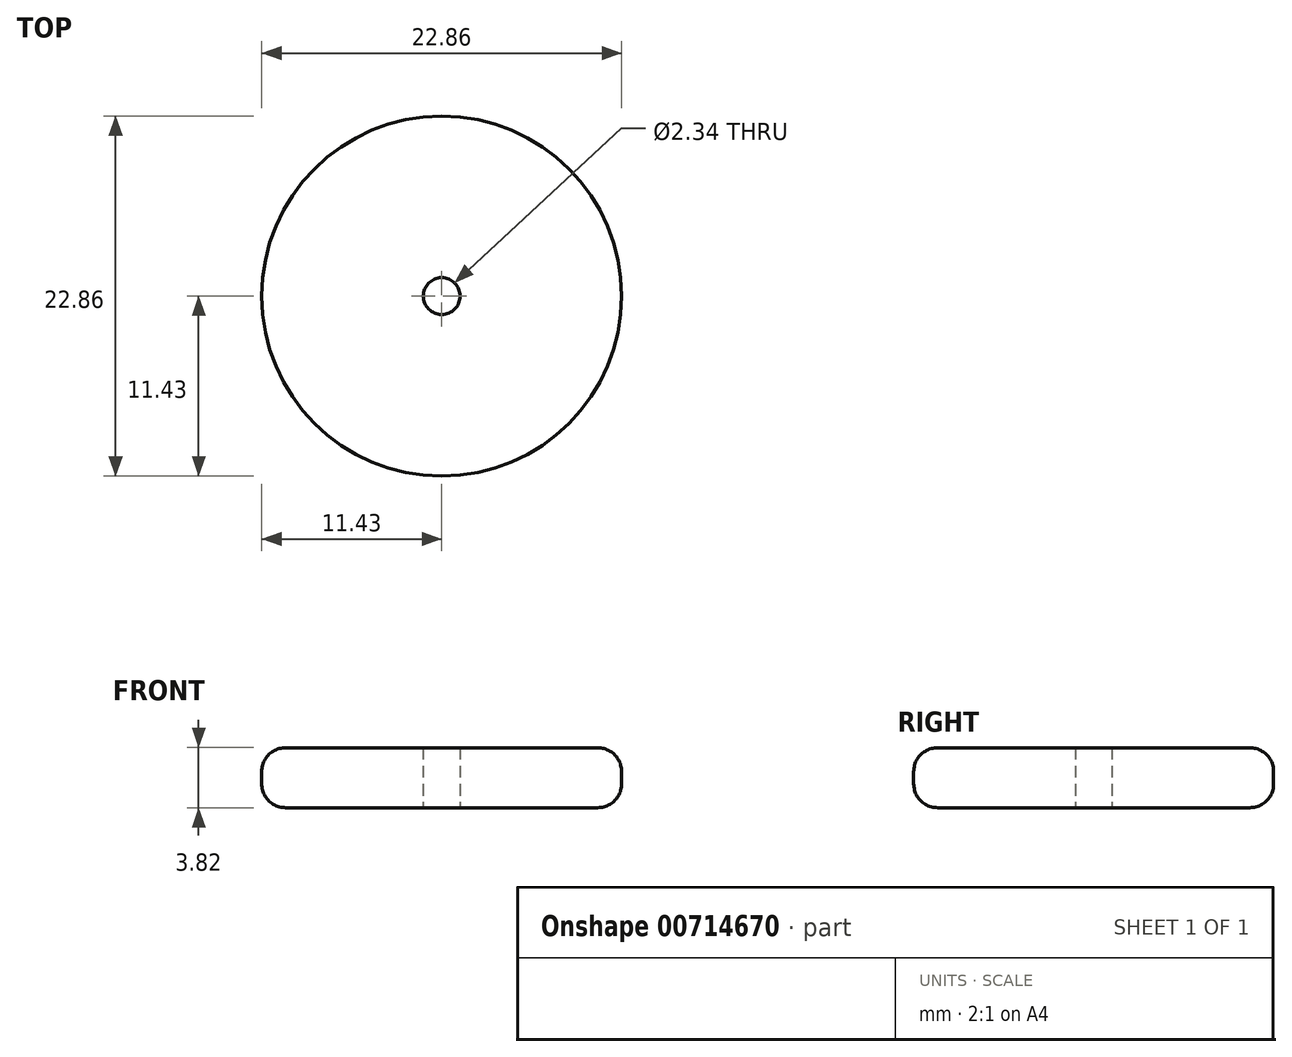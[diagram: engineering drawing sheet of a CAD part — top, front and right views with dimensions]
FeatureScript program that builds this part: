
annotation { "Feature Type Name" : "Feature", "Feature Type Description" : "" }
export const myFeature = defineFeature(function(context is Context, id is Id, definition is map)
    precondition{}
    {
        {
            var Q0;
            Q0=qCreatedBy(makeId("Top.planeOp"),FACE);
            var sketch = newSketch(context, id + "F0", { "sketchPlane" : qUnion([Q0])});
            skPoint(sketch, "E0.center.orphan", {"position": v(0, 0) * mm});
            skPoint(sketch, "E1.start.orphan", {"position": v(11.43, 0) * mm});
            skCircle(sketch, "E2", {"center": v(0, 0) * mm, "radius": 11.43 * mm});
            skSolve(sketch);
        }
        {
            var Q0;
            Q0 = qSketchRegion(id + "F0", true);
            extrude(context, id + "F1", {"entities" : qUnion([Q0]), "depth" : 3.8 * mm, "offsetDistance" : 25.4 * mm, "symmetric" : true});
        }
        {
            var Q0;
            Q0=makeQuery(id+"F1.opExtrude","CAP_FACE",FACE,{"disambiguationData":[OSD([sQuery(id+"F0.wireOp",EDGE,"E2")])],"isStart":true});
            var sketch = newSketch(context, id + "F2", { "sketchPlane" : qUnion([Q0])});
            skCircle(sketch, "E3", {"center": v(0, 0) * mm, "radius": 1.17 * mm});
            skSolve(sketch);
        }
        {
            var Q0;
            Q0=makeQuery(id+"F2.imprint","IMPRINT",FACE,{"disambiguationData":[TD([[makeQuery(id+"F2.imprint","IMPRINT",EDGE,{"derivedFrom":sQuery(id+"F2.wireOp",EDGE,"E3")}),1.0]])]});
            extrude(context, id + "F3", {"entities" : qUnion([Q0]), "operationType" : NewBodyOperationType.REMOVE, "oppositeDirection" : true, "depth" : 25.4 * mm, "offsetDistance" : 25.4 * mm});
        }
        {
            var Q0;
            Q0=makeQuery(id+"F1.opExtrude","CAP_EDGE",EDGE,{"disambiguationData":[OSD([sQuery(id+"F0.wireOp",EDGE,"E2")])],"isStart":false});
            var Q1;
            Q1=makeQuery(id+"F1.opExtrude","CAP_EDGE",EDGE,{"disambiguationData":[OSD([sQuery(id+"F0.wireOp",EDGE,"E2")])],"isStart":true});
            fillet(context, id + "F4", {"entities" : qUnion([Q0, Q1]), "radius" : 1.52 * mm, "tangentPropagation" : true, "allowEdgeOverflow" : false});
        }
    });
